# Revit family: Grohe_PlumbingFixture_ConcealedBody_SingleLeverMixer_23571000
name_source: partatom
category: Plumbing Fixtures
revit_build: Autodesk Revit 2018 (Build: 20190510_1515(x64)
units: mm (PartAtom-declared; Revit-internal decimal feet)

## family parameters
Cut with Voids When Loaded = No
Host = Face
OmniClass Number = 23.45.55.11
OmniClass Title = Sanitary Components
Part Type = Normal
Room Calculation Point = No
Round Connector Dimension = Use Diameter
Shared = No

## types (1)
- 23571000
    Assembly Code = D2010
    AssetType = Fixed
    BIMObjectName = Grohe_PlumbingFixture_ConcealedBody_SingleLeverMixer_23571000
    ClassificationName = Uniclass2015
    ClassificationValue = Pr_40_20_87_96
    Cost = 0 $
    Default Elevation = 1219 mm
    Description = or 2-hole basin mixers wall installation without finishing trim set GROHE SilkMove 35 mm ceramic cartridge adjustable flow rate limiter, with temperature limiter spout can be positioned on the right or left, installation depth 45 to 75 mm. DR-brass, installation device allows for waterproofing of wall construction surrounding the concealed body with sealing sleeve
    DocumentationCertificates = https://www.bimstore.co
    DocumentationInstallationGuide = https://www.bimstore.co
    DocumentationLiterature = https://www.bimstore.co
    DocumentationMaintenance = https://www.bimstore.co
    DocumentationTechnical = https://www.bimstore.co
    DurationUnit = Years
    ExpectedLife = 0
    IfcExportAs = IfcPipeFitting
    IfcExportType = IfcPipeFittingType
    Keynote = N13
    Manufacturer = Grohe
    ManufacturerName = Grohe
    Model = Single-lever mixer 1/2", universal concealed body
    ModelNumber = 23571000
    ModelReference = Single-lever mixer 1/2", universal concealed body
    NBSDescription = Water supply fittings for wash basins and troughs
    NBSObjectName = Grohe - Water supply fittings for wash basins and troughs
    NBSReference = 45-35-70/371
    NominalDepth = 0 mm  [stored 0 ft]
    NominalHeight = 0 mm  [stored 0 ft]
    NominalLength = 0 mm  [stored 0 ft]
    ProductionYear = 2020
    ReplacementCost = 0
    Type Comments = 23571000
    TypeName = 23571000
    URL = https://pro.grohe.com
    WarrantyDurationLabor = 0
    WarrantyDurationParts = 0
    WarrantyDurationUnit = Years
    _BSBibleVersion = 16
    _BimSpecGuid = 0
    _CurrentRevision = 1
    _DistributedBy = www.bimstore.co
    _ObjectUserGuide = https://www.bimstore.co

note: [stored X ft] marks values corroborated as IEEE doubles in the binary element streams (Revit-internal decimal feet)

## geometry (parser evidence)
native form markers: Sweep x2
no freeform markers — native parametric forms only
